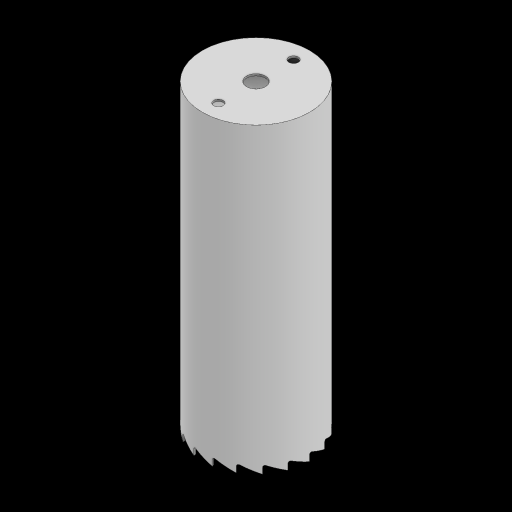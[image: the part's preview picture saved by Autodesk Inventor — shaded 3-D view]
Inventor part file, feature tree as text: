
AUTODESK INVENTOR PART (.ipt)
format: ipt  version: 2023 (Build 270158000, 158)  size: 222,720 bytes
history: native  units: in
note: dims shown in document units (in); Inventor stores cm internally (conversion verified against a paired STEP export)
features: extrude x5, sketch x3, pattern_circular x2, plane x1, fillet x1
ambient origin geometry x8: Origin, YZ Plane, XZ Plane, XY Plane, X Axis, Y Axis, Z Axis, Center Point
bodies: Body1 (feature_tree)
feature tree (12):
  sketch  "Sketch1"  dims[d0=1.375in d4=1.425in]
  extrude  "Extrusion2"  Depth=1.425in
  extrude  "Extrusion3"  Depth=0.025in TaperAngle=0.0deg
  sketch  "Sketch3"  dims[d5=4.0in d6=0.0in d7=0.025in d8=0.0in]
  extrude  "Extrusion4"  TaperAngle=0.0deg  [1 undecoded]
  plane  "Work Plane1"
  extrude  "Extrusion5"  Depth=0.022in
  pattern_circular  "Circular Pattern1"  [2 undecoded]
  fillet  "Face Fillet1"
  pattern_circular  "Circular Pattern2"  [2 undecoded]
  extrude  "Extrusion6"  TaperAngle=0.0deg  [1 undecoded]
  sketch  "Sketch5"  dims[d9=0.25in d10=0.0in d11=0.0in d12=0.7125in d13=0.125in d14=0.125in d17=0.0in d18=0.0in d19=0.115in d20=7.0866in d21=360.0deg d23=0.022in d42=7.0866in d43=360.0deg d45=0.125in d46=0.125in d47=0.5in d48=0.5in d49=1.0in d50=0.0in d1=0.5in d2=0.0344in d3=0.5in d15=0.0344in d24=0.0in d25=0.0in d26=0.0in]
note: 6 required parameter values undecoded (feature->parameter linkage not recoverable at this tier; creation-order binding heuristic only, values carry confidence <= 0.55)
